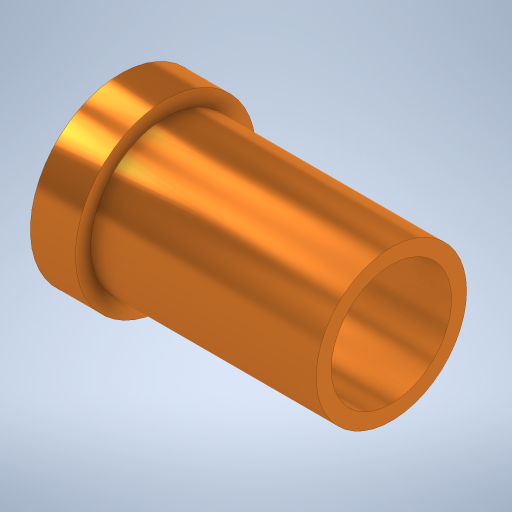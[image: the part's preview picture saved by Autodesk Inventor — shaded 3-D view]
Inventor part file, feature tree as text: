
AUTODESK INVENTOR PART (.ipt)
format: ipt  version: 2024 (Build 280153000, 153)  size: 281,600 bytes
history: native  units: mm
features: sketch x2, revolve x1, hole x1
ambient origin geometry x8: Origin, YZ Plane, XZ Plane, XY Plane, X Axis, Y Axis, Z Axis, Center Point
bodies: Volumenkörper1 (feature_tree)
feature tree (4):
  revolve  "Umdrehung1"
  hole  "Bohrung1"  [1 undecoded]
  sketch  "Skizze1"  dims[d0=1.5mm d1=6.0mm]
  sketch  "Skizze2"  dims[d2=5.0mm d3=9.0mm d4=90.0deg d5=4.0mm d6=10.0mm d7=4.0mm d8=2.0mm d9=90.0deg d10=8.0mm d11=20.594885mm]
note: 1 required parameter value undecoded (feature->parameter linkage not recoverable at this tier; creation-order binding heuristic only, values carry confidence <= 0.55)
